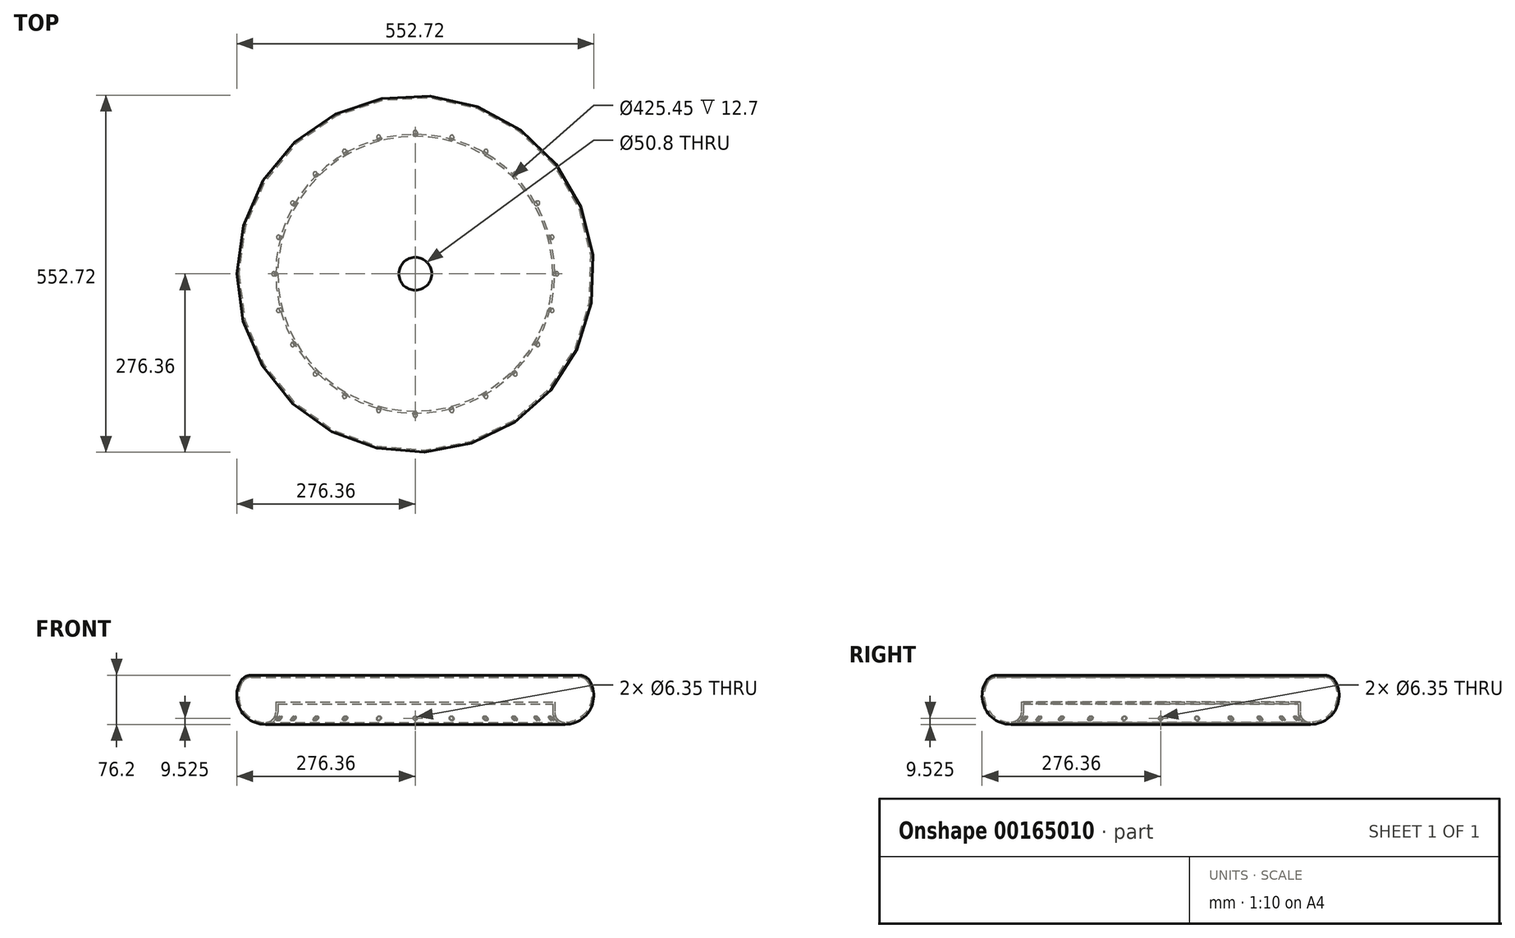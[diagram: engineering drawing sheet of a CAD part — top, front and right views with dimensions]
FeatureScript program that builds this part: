
annotation { "Feature Type Name" : "Feature", "Feature Type Description" : "" }
export const myFeature = defineFeature(function(context is Context, id is Id, definition is map)
    precondition{}
    {
        {
            var Q0;
            Q0=qCreatedBy(makeId("Front.planeOp"),FACE);
            var sketch = newSketch(context, id + "F0", { "sketchPlane" : qUnion([Q0])});
            skLineSegment(sketch, "E0.bottom", {"start": v(0, 0) * mm, "end": v(212.72, 0) * mm});
            skLineSegment(sketch, "E0.top", {"start": v(0, 3.18) * mm, "end": v(215.9, 3.18) * mm});
            skLineSegment(sketch, "E0.left", {"start": v(0, 0) * mm, "end": v(0, 3.18) * mm});
            skLineSegment(sketch, "E1", {"start": v(254, 41.28) * mm, "end": v(0, 41.28) * mm});
            skLineSegment(sketch, "E2", {"start": v(0, 41.28) * mm, "end": v(0, 44.45) * mm});
            skLineSegment(sketch, "E3", {"start": v(0, 44.45) * mm, "end": v(254, 44.45) * mm});
            skLineSegment(sketch, "E4", {"start": v(0, 3.18) * mm, "end": v(0, 41.28) * mm, "construction": true});
            skLineSegment(sketch, "E5", {"start": v(215.9, 3.17) * mm, "end": v(215.9, -12.7) * mm});
            skLineSegment(sketch, "E6", {"start": v(212.72, 0) * mm, "end": v(212.72, -12.7) * mm});
            skLineSegment(sketch, "E7", {"start": v(212.72, -12.7) * mm, "end": v(215.9, -12.7) * mm, "construction": true});
            skLineSegment(sketch, "E8", {"start": v(254, 44.45) * mm, "end": v(254, 41.28) * mm, "construction": true});
            skArc(sketch, "E9", {"start": v(267.82, 33.21) * mm, "mid": v(262, 39.11) * mm, "end": v(254, 41.28) * mm});
            skArc(sketch, "E10", {"start": v(270.58, 34.78) * mm, "mid": v(263.6, 41.85) * mm, "end": v(254, 44.45) * mm});
            skArc(sketch, "E11", {"start": v(212.72, -12.7) * mm, "mid": v(218.3, -26.17) * mm, "end": v(231.78, -31.75) * mm});
            skArc(sketch, "E12", {"start": v(215.9, -12.7) * mm, "mid": v(220.55, -23.93) * mm, "end": v(231.77, -28.58) * mm});
            skArc(sketch, "E13", {"start": v(231.77, -28.58) * mm, "mid": v(267.54, -8.03) * mm, "end": v(267.82, 33.21) * mm});
            skArc(sketch, "E14", {"start": v(231.78, -31.75) * mm, "mid": v(270.28, -9.63) * mm, "end": v(270.58, 34.78) * mm});
            skLineSegment(sketch, "E15", {"start": v(270.58, 34.78) * mm, "end": v(267.82, 33.21) * mm, "construction": true});
            skLineSegment(sketch, "E16", {"start": v(231.77, -28.58) * mm, "end": v(231.78, -31.75) * mm, "construction": true});
            skLineSegment(sketch, "E17", {"start": v(231.78, -31.75) * mm, "end": v(0, -31.75) * mm, "construction": true});
            skLineSegment(sketch, "E18", {"start": v(0, -31.75) * mm, "end": v(0, 0) * mm, "construction": true});
            skLineSegment(sketch, "E19", {"start": v(254, 25.4) * mm, "end": v(231.78, 12.83) * mm, "construction": true});
            skLineSegment(sketch, "E20", {"start": v(231.78, -12.7) * mm, "end": v(231.78, 12.83) * mm, "construction": true});
            skLineSegment(sketch, "E21.top", {"start": v(254, 3.18) * mm, "end": v(215.9, 3.18) * mm, "construction": true});
            skLineSegment(sketch, "E21.left", {"start": v(254, 41.28) * mm, "end": v(254, 3.18) * mm, "construction": true});
            skSolve(sketch);
        }
        {
            var Q0;
            Q0=qCreatedBy(makeId("Top.planeOp"),FACE);
            var sketch = newSketch(context, id + "F1", { "sketchPlane" : qUnion([Q0])});
            skCircle(sketch, "E22", {"center": v(0, 0) * mm, "radius": 25.4 * mm});
            skSolve(sketch);
        }
        {
            var Q0;
            Q0=qSketchRegion(id+"F0",true);
            var Q1;
            Q1=sQuery(id+"F1.wireOp",EDGE,"E22");
            revolve(context, id + "F2", {"entities" : qUnion([Q0]), "axis" : qUnion([Q1]), "revolveType" : RevolveType.FULL});
        }
        {
            var Q0;
            Q0=qCreatedBy(makeId("Front.planeOp"),FACE);
            var sketch = newSketch(context, id + "F3", { "sketchPlane" : qUnion([Q0])});
            skLineSegment(sketch, "E23", {"start": v(0, -12.7) * mm, "end": v(0, -22.23) * mm, "construction": true});
            skCircle(sketch, "E24", {"center": v(0, -22.23) * mm, "radius": 3.18 * mm});
            skSolve(sketch);
        }
        {
            var Q0;
            Q0=qSketchRegion(id+"F3",true);
            var Q1;
            Q1=makeQuery(id+"F2.opRevolve","SWEPT_FACE",FACE,{"disambiguationData":[OSD([sQuery(id+"F0.wireOp",EDGE,"E12")])]});
            extrude(context, id + "F4", {"entities" : qUnion([Q0]), "operationType" : NewBodyOperationType.REMOVE, "endBound" : BoundingType.UP_TO_SURFACE, "oppositeDirection" : true, "endBoundEntityFace" : qUnion([Q1]), "depth" : 25.4 * mm});
        }
        {
            var Q0;
            Q0=makeQuery(id+"F4.boolean.opBoolean","COPY",FACE,{"derivedFrom":makeQuery(id+"F4.opExtrude","SWEPT_FACE",FACE,{"disambiguationData":[OSD([sQuery(id+"F3.wireOp",EDGE,"E24")])]})});
            var Q1;
            Q1=makeQuery(id+"F2.opRevolve","SWEPT_FACE",FACE,{"disambiguationData":[OSD([sQuery(id+"F0.wireOp",EDGE,"E13")])]});
            circularPattern(context, id + "F5", {"patternType" : PatternType.FACE, "faces" : qUnion([Q0]), "axis" : qUnion([Q1]), "angle" : 360 * degree, "instanceCount" : 24, "equalSpace" : true});
        }
        {
            var Q0;
            Q0=makeQuery(id+"F2.opRevolve","SWEPT_FACE",FACE,{"disambiguationData":[OSD([sQuery(id+"F0.wireOp",EDGE,"E3")])]});
            var sketch = newSketch(context, id + "F6", { "sketchPlane" : qUnion([Q0])});
            skCircle(sketch, "E25", {"center": v(0, 0) * mm, "radius": 25.4 * mm});
            skSolve(sketch);
        }
        {
            var Q0;
            Q0 = qSketchRegion(id + "F6", true);
            extrude(context, id + "F7", {"entities" : qUnion([Q0]), "operationType" : NewBodyOperationType.REMOVE, "oppositeDirection" : true, "depth" : 3.17 * mm});
        }
    });
